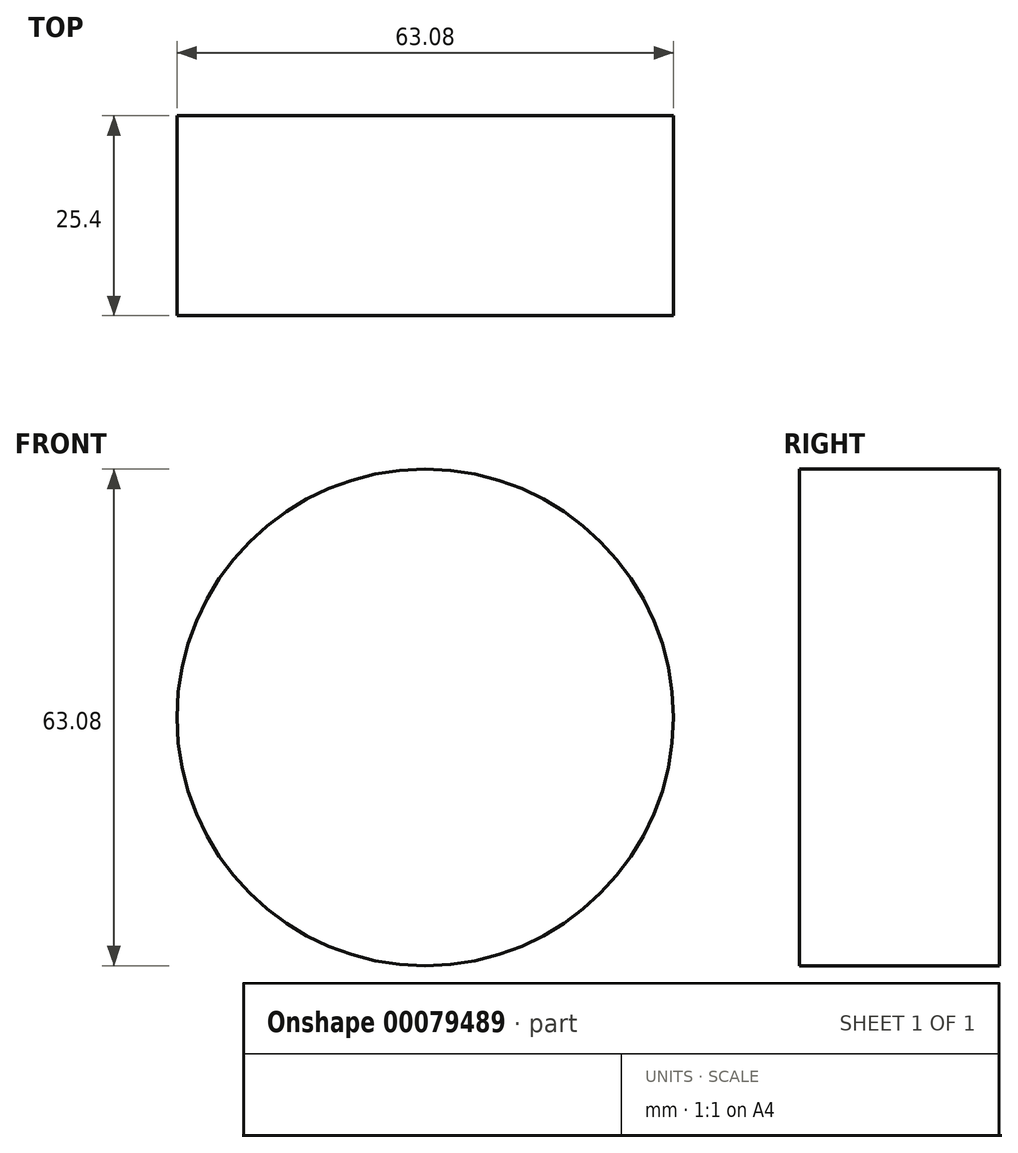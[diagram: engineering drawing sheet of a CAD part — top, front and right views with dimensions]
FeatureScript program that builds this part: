
annotation { "Feature Type Name" : "Feature", "Feature Type Description" : "" }
export const myFeature = defineFeature(function(context is Context, id is Id, definition is map)
    precondition{}
    {
        {
            var Q0;
            Q0=qCreatedBy(makeId("Front.planeOp"),FACE);
            var sketch = newSketch(context, id + "F0", { "sketchPlane" : qUnion([Q0])});
            skCircle(sketch, "E0", {"center": v(0, 0) * mm, "radius": 31.54 * mm});
            skSolve(sketch);
        }
        {
            var Q0;
            Q0=makeQuery(id+"F0.imprint","IMPRINT",FACE,{"disambiguationData":[TD([[makeQuery(id+"F0.imprint","IMPRINT",EDGE,{"derivedFrom":sQuery(id+"F0.wireOp",EDGE,"E0")}),1.0]])]});
            extrude(context, id + "F1", {"entities" : qUnion([Q0]), "depth" : 25.4 * mm});
        }
    });
